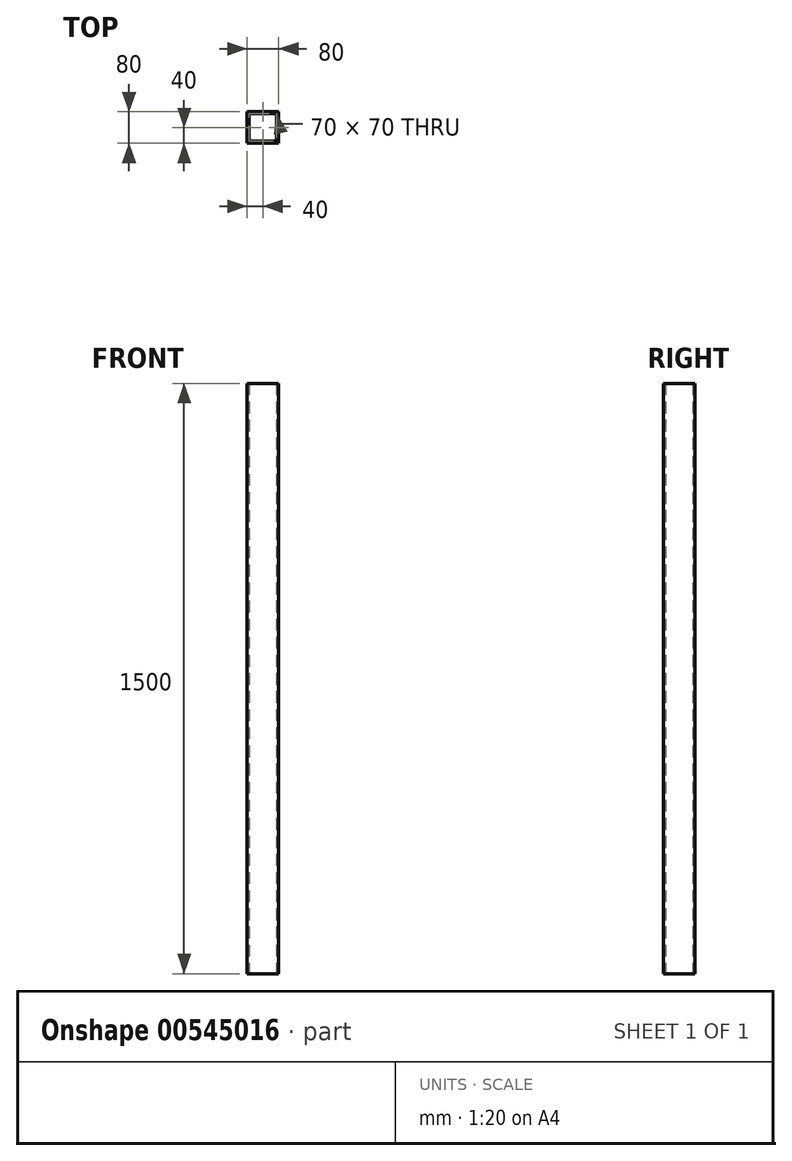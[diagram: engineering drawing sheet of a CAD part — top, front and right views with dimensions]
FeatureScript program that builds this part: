
annotation { "Feature Type Name" : "Feature", "Feature Type Description" : "" }
export const myFeature = defineFeature(function(context is Context, id is Id, definition is map)
    precondition{}
    {
        {
            var Q0;
            Q0=qCreatedBy(makeId("Top.planeOp"),FACE);
            var sketch = newSketch(context, id + "F0", { "sketchPlane" : qUnion([Q0])});
            skLineSegment(sketch, "E0.bottom", {"start": v(-40, 40) * mm, "end": v(40, 40) * mm});
            skLineSegment(sketch, "E0.top", {"start": v(-40, -40) * mm, "end": v(40, -40) * mm});
            skLineSegment(sketch, "E0.left", {"start": v(-40, 40) * mm, "end": v(-40, -40) * mm});
            skLineSegment(sketch, "E0.right", {"start": v(40, 40) * mm, "end": v(40, -40) * mm});
            skPoint(sketch, "E0.middle", {"position": v(0, 0) * mm});
            skLineSegment(sketch, "E1.bottom", {"start": v(35, 35) * mm, "end": v(-35, 35) * mm});
            skLineSegment(sketch, "E1.top", {"start": v(35, -35) * mm, "end": v(-35, -35) * mm});
            skLineSegment(sketch, "E1.left", {"start": v(35, 35) * mm, "end": v(35, -35) * mm});
            skLineSegment(sketch, "E1.right", {"start": v(-35, 35) * mm, "end": v(-35, -35) * mm});
            skSolve(sketch);
        }
        {
            var Q0;
            Q0=makeQuery(id+"F0.imprint","IMPRINT",FACE,{"disambiguationData":[TD([[makeQuery(id+"F0.imprint","IMPRINT",EDGE,{"derivedFrom":sQuery(id+"F0.wireOp",EDGE,"E0.bottom")}),-1.0]])]});
            extrude(context, id + "F1", {"entities" : qUnion([Q0]), "endBound" : BoundingType.SYMMETRIC, "depth" : 1500 * mm, "offsetDistance" : 25 * mm});
        }
    });
